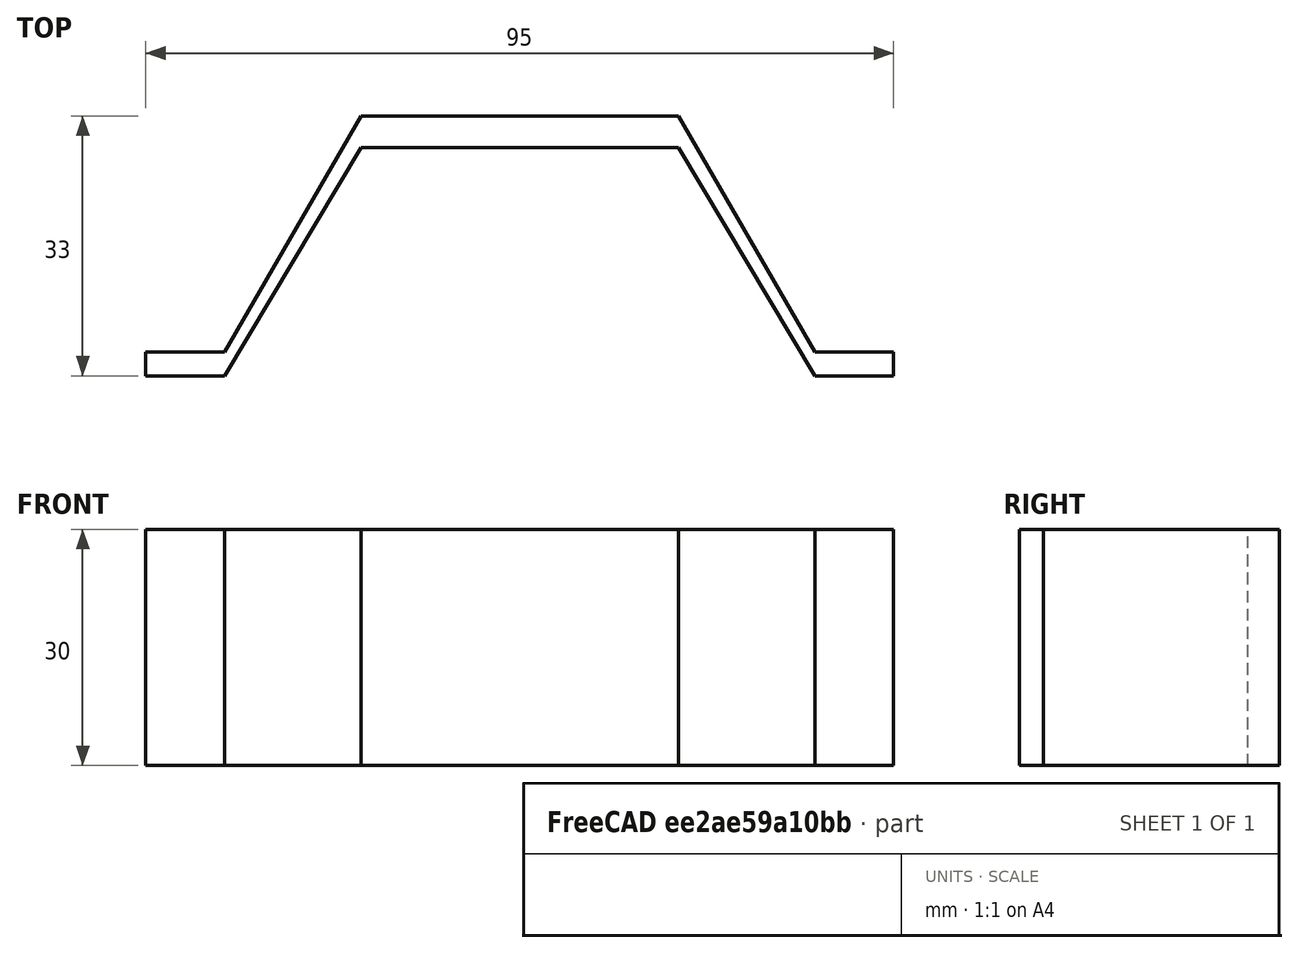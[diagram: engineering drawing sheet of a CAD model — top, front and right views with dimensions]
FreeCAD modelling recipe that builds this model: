
FCSTD DOCUMENT  (FreeCAD 0.22R38261 (Git))
Label: ручка
License: All rights reserved
LicenseURL: https://en.wikipedia.org/wiki/All_rights_reserved
objects: Sketcher::SketchObject×1, PartDesign::Pad×1, PartDesign::Body×1
note: 5 computed .brp shape members not serialized (recipe doc carries the construction recipe); baked Part::Feature solids carry a one-line shape summary decoded from their .brp

FEATURE [Sketcher::SketchObject] Sketch
  AttachmentSupport = -> [XY_Plane]
  FullyConstrained = true
  MapMode = 5
  sketch-geometry (12):
    g0: LineSegment StartX=0 StartY=0 StartZ=0 EndX=-10 EndY=0 EndZ=0
    g1: LineSegment StartX=0 StartY=0 StartZ=0 EndX=17.3205 EndY=30 EndZ=0
    g2: LineSegment StartX=17.3205 StartY=30 StartZ=0 EndX=57.6795 EndY=30 EndZ=0
    g3: LineSegment StartX=57.6795 StartY=30 StartZ=0 EndX=75 EndY=0 EndZ=0
    g4: LineSegment StartX=75 StartY=0 StartZ=0 EndX=85 EndY=0 EndZ=0
    g5: LineSegment StartX=-10 StartY=0 StartZ=0 EndX=-10 EndY=-3 EndZ=0
    g6: LineSegment StartX=-10 StartY=-3 StartZ=0 EndX=0 EndY=-3 EndZ=0
    g7: LineSegment StartX=0 StartY=-3 StartZ=0 EndX=17.3205 EndY=26 EndZ=0
    g8: LineSegment StartX=17.3205 StartY=26 StartZ=0 EndX=57.6795 EndY=26 EndZ=0
    g9: LineSegment StartX=57.6795 StartY=26 StartZ=0 EndX=75 EndY=-3 EndZ=0
    g10: LineSegment StartX=75 StartY=-3 StartZ=0 EndX=85 EndY=-3 EndZ=0
    g11: LineSegment StartX=85 StartY=-3 StartZ=0 EndX=85 EndY=0 EndZ=0
  constraints (35):
    c: Coincident(g0,g-1)
    c: Coincident(g1,g0)
    c: Horizontal(g2)
    c: PointOnObject(g3,g-1)
    c: Coincident(g4,g3)
    c: PointOnObject(g4,g-1)
    c: DistanceX(g4,g4) = 10
    c: DistanceX(g0,g0) = 10
    c: DistanceX(g0,g4) = 95
    c: Coincident(g2,g1)
    c: Coincident(g3,g2)
    c: Angle(g2,g3) = 2.0944
    c: Angle(g1,g2) = 2.0944
    c: DistanceY(g0,g1) = 30
    c: PointOnObject(g0,g-1)
    c: Coincident(g5,g0)
    c: Coincident(g6,g5)
    c: PointOnObject(g6,g-2)
    c: Horizontal(g8)
    c: Coincident(g9,g8)
    c: Coincident(g10,g9)
    c: Coincident(g11,g4)
    c: Vertical(g9,g3)
    c: Vertical(g11)
    c: Coincident(g10,g11)
    c: Vertical(g5)
    c: Horizontal(g5,g6)
    c: Horizontal(g6,g9)
    c: Horizontal(g9,g10)
    c: DistanceY(g5,g0) = 3
    c: Coincident(g7,g8)
    c: DistanceY(g8,g2) = 4
    c: Coincident(g7,g6)
    c: Vertical(g7,g1)
    c: Vertical(g8,g2)
FEATURE [PartDesign::Pad] Pad
  Direction = (0,0,1)
  Length = 30
  Length2 = 10
  Profile = -> Sketch
  ReferenceAxis = -> Sketch [N_Axis]
  Suppressed = false
  Type = 0
FEATURE [PartDesign::Body] Body  label="Тело"
  AllowCompound = false
  Group = -> [Sketch,Pad]
  Origin = -> Origin
  Tip = -> Pad
